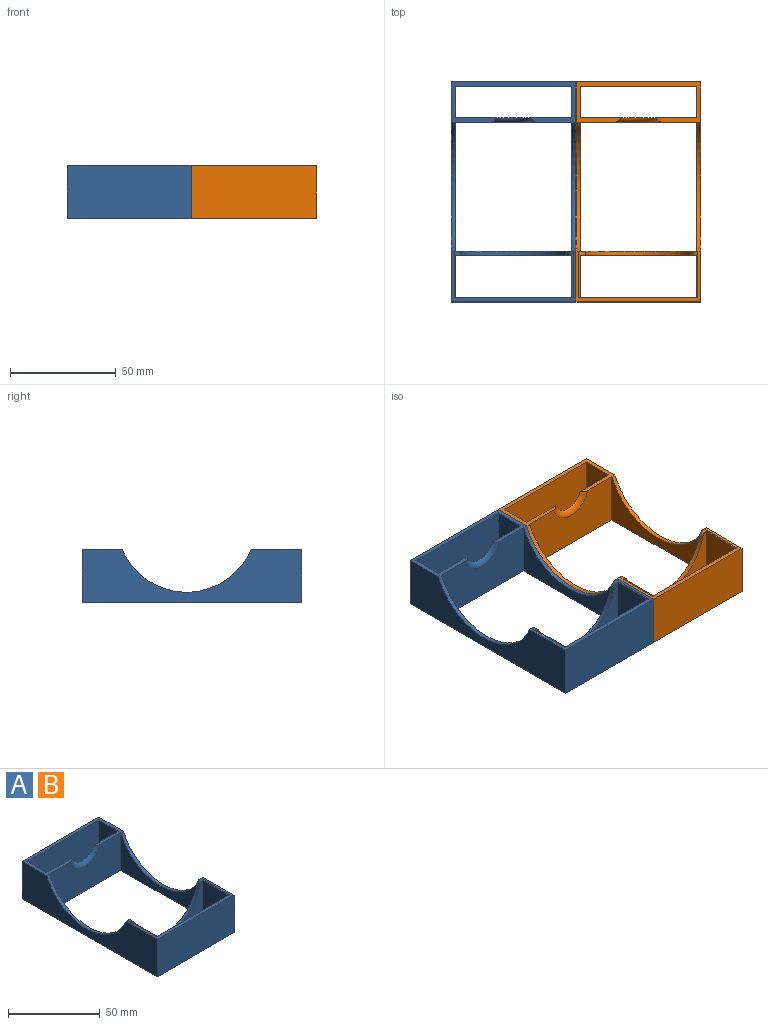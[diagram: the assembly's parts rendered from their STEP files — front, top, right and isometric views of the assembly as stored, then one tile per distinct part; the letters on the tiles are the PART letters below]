
ASSEMBLY  parts=2 mates=1
PART A: 25 faces, bbox 59x104x25.8 mm
  f0: plane 59x19mm, normal (0,0,1), area 259.4mm2, adj f4,f8,f9,f10,f12,f14,f15,f16
  f1: plane 61x25mm, normal (1,0,0), area 637.3mm2, adj f4,f11,f18,f21,f23
  f2: plane 59x24mm, normal (0,0,1), area 178.9mm2, adj f6,f12,f13,f14,f20,f21,f23,f24
  f3: plane 61x25mm, normal (-1,0,0), area 637.3mm2, adj f4,f11,f18,f20,f24
  f4: plane 55x25mm, normal (0,-1,0), area 1229.3mm2, adj f0,f1,f3,f18,f22
  f5: plane 55x24.94mm, normal (0,-1,0), area 485.1mm2, adj f7,f17,f18,f19,f23,f24
  f6: plane 56.23x25mm, normal (0,1,0), area 1375mm2, adj f2,f7,f17,f18,f23,f24
  f7: plane 24.94x20mm, normal (1,0,0), area 498.7mm2, adj f5,f6,f18,f23
  f8: plane 55x25mm, normal (0,1,0), area 1303.5mm2, adj f0,f9,f15,f18,f22
  f9: plane 25x15mm, normal (1,0,0), area 375mm2, adj f0,f8,f10,f18
  f10: plane 55x25mm, normal (0,-1,0), area 1375mm2, adj f0,f9,f15,f18
  f11: plane 55x24.94mm, normal (0,1,0), area 485.1mm2, adj f1,f3,f18,f19,f23,f24
  f12: plane 104x25mm, normal (-1,0,0), area 1712.3mm2, adj f0,f2,f13,f16,f18,f21
  f13: plane 59x25mm, normal (0,-1,0), area 1475mm2, adj f2,f12,f14,f18
  f14: plane 104x25mm, normal (1,0,0), area 1712.3mm2, adj f0,f2,f13,f16,f18,f20
  f15: plane 25x15mm, normal (-1,0,0), area 375mm2, adj f0,f8,f10,f18
  f16: plane 59x25mm, normal (0,1,0), area 1475mm2, adj f0,f12,f14,f18
  f17: plane 24.94x20mm, normal (-1,0,0), area 498.7mm2, adj f5,f6,f18,f24
  f18: plane 104x59mm, normal (0,0,-1), area 856mm2, adj f1,f3,f4,f5,f6,f7,f8,f9
  f19: cylinder r=25.75mm len=50.37mm, axis (0,-1,0), area 140.1mm2, adj f5,f11,f23,f24
  f20: cylinder r=33.15mm len=61mm, axis (-1,0,0), area 154.9mm2, adj f0,f2,f3,f14,f24
  f21: cylinder r=33.15mm len=61mm, axis (1,0,0), area 154.9mm2, adj f0,f1,f2,f12,f23
  f22: torus R=11.7mm, axis (0,1,0), area 94.4mm2, adj f0,f4,f8
  f23: cylinder r=3mm len=22.03mm, axis (0,-1,0), area 20.6mm2, adj f1,f2,f5,f6,f7,f11,f19,f21
  f24: cylinder r=3mm len=22.03mm, axis (0,-1,0), area 20.6mm2, adj f2,f3,f5,f6,f11,f17,f19,f20
PART B: same geometry as A
PLACE A t=(-15.92,24.05,-9.79)mm
PLACE B t=(43.08,24.05,-9.79)mm
MATE planar B.f12 <-> A.f14  axis (-1,0,0) through (36.83,23.45,0.54)mm
